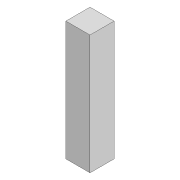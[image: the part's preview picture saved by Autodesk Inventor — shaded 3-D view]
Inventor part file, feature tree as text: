
AUTODESK INVENTOR PART (.ipt)
format: ipt  version: 2022 (Build 260153000, 153)  size: 77,824 bytes
history: native  units: mm
features: extrude x1, sketch x1
ambient origin geometry x8: Origin, YZ Plane, XZ Plane, XY Plane, X Axis, Y Axis, Z Axis, Center Point
bodies: Solid1 (feature_tree)
feature tree (2):
  extrude  "Extrusion1"  Depth=20.2mm
  sketch  "Sketch1"  dims[d0=20.2mm d1=20.2mm d2=100.0mm d3=0.0mm]
